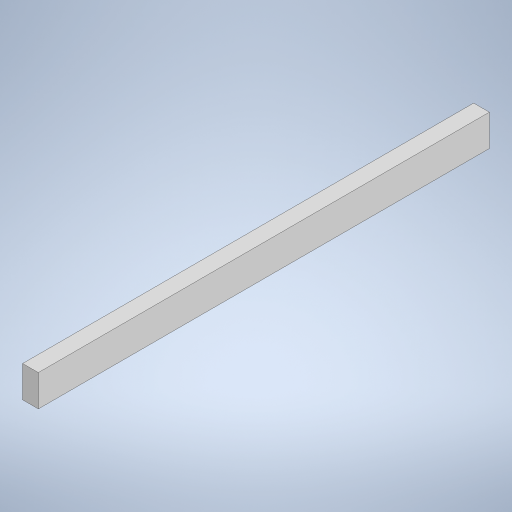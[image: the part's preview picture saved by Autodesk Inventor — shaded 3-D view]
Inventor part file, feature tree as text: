
AUTODESK INVENTOR PART (.ipt)
format: ipt  version: 2023 (Build 270158000, 158)  size: 229,376 bytes
history: native  units: mm
features: extrude x1, sketch x1
ambient origin geometry x8: Origin, YZ Plane, XZ Plane, XY Plane, X Axis, Y Axis, Z Axis, Center Point
bodies: Solid1 (feature_tree)
feature tree (2):
  extrude  "Extrusion1"  Depth=15.0mm
  sketch  "Sketch1"  dims[d0=30.0mm d1=15.0mm d2=430.0mm d3=0.0mm]
